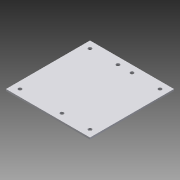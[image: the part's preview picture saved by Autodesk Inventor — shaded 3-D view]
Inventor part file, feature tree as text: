
AUTODESK INVENTOR PART (.ipt)
format: ipt  version: 2015 SP1 (Build 190203100, 203)  size: 111,616 bytes
history: native  units: in
note: dims shown in document units (in); Inventor stores cm internally (conversion verified against a paired STEP export)
features: sketch x3, hole x2, extrude x1
ambient origin geometry x8: Origin, YZ Plane, XZ Plane, XY Plane, X Axis, Y Axis, Z Axis, Center Point
bodies: Solid1 (feature_tree)
feature tree (6):
  extrude  "Extrusion1"  Depth=6.0in
  hole  "Hole1"  [1 undecoded]
  hole  "Hole2"  [1 undecoded]
  sketch  "Sketch1"  dims[d0=6.0in d1=6.0in]
  sketch  "Sketch2"  dims[d2=0.125in d3=0.0in d4=0.5in]
  sketch  "Sketch3"  dims[d5=0.5in d6=0.5in d7=0.5in d8=0.5in d9=0.5in d10=0.5in d11=2.5in d12=0.5in d13=0.5in d14=0.5in d15=2.5in d16=0.25in d17=0.75in d18=0.375in d19=0.25in d20=0.5635in d21=1.0in d22=0.8108in d23=0.5in d24=2.0in d25=0.25in d26=0.75in d27=0.375in d28=0.25in d29=0.5635in d30=1.0in d31=0.8108in]
note: 2 required parameter values undecoded (feature->parameter linkage not recoverable at this tier; creation-order binding heuristic only, values carry confidence <= 0.55)
